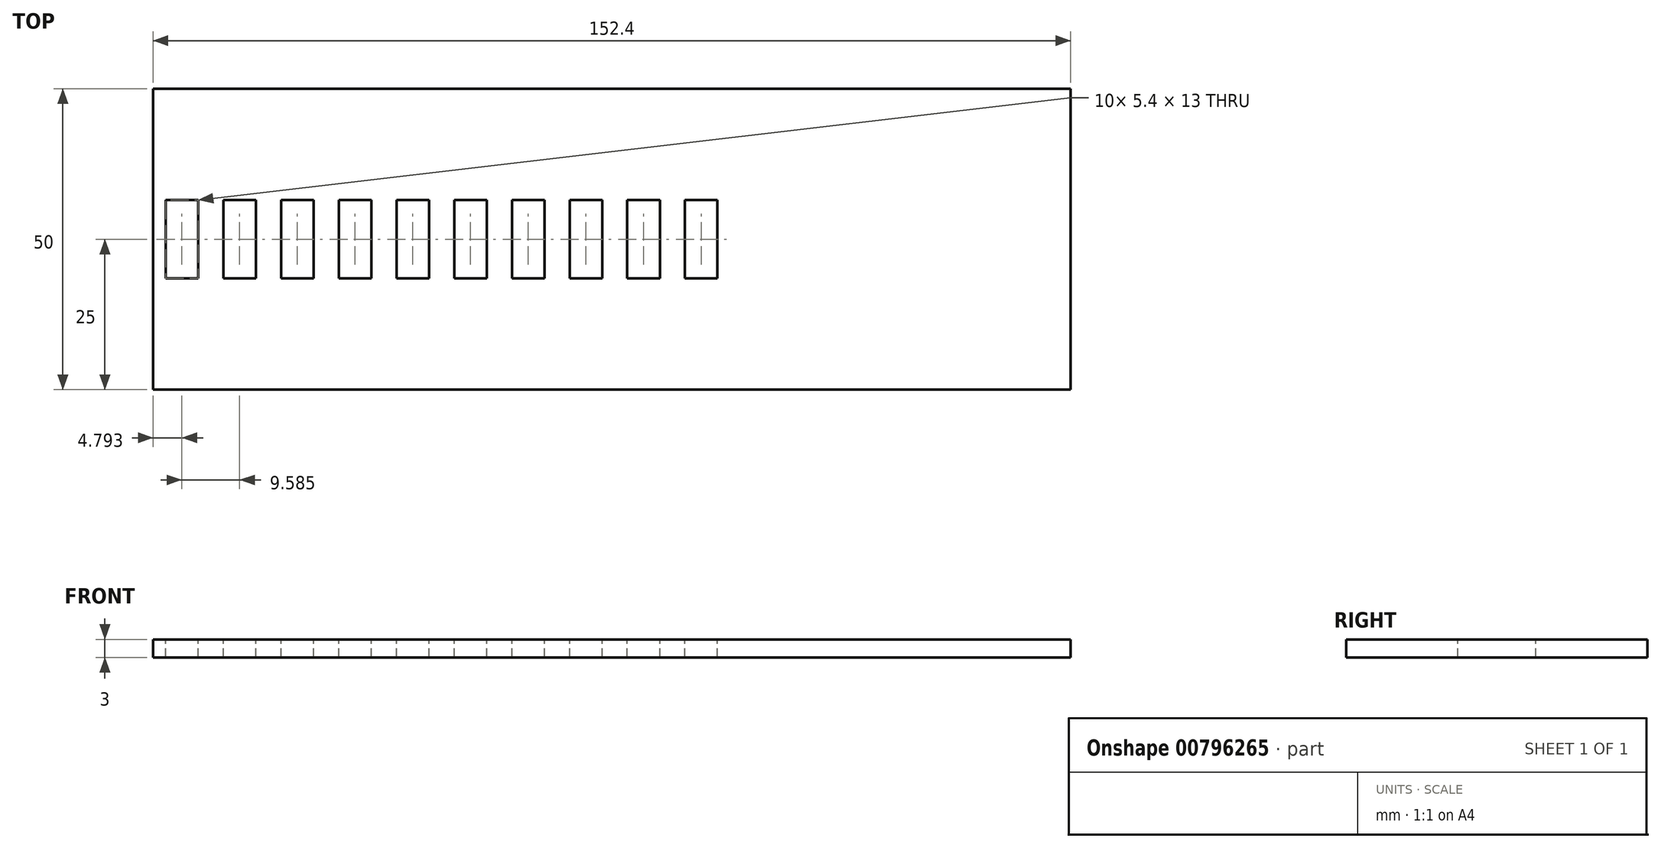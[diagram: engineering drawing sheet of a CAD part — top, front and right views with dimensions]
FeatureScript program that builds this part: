
annotation { "Feature Type Name" : "Feature", "Feature Type Description" : "" }
export const myFeature = defineFeature(function(context is Context, id is Id, definition is map)
    precondition{}
    {
        {
            var Q0;
            Q0=qCreatedBy(makeId("Top.planeOp"),FACE);
            var sketch = newSketch(context, id + "F0", { "sketchPlane" : qUnion([Q0])});
            skLineSegment(sketch, "E0.bottom", {"start": v(76.2, -25) * mm, "end": v(-76.2, -25) * mm});
            skLineSegment(sketch, "E0.top", {"start": v(76.2, 25) * mm, "end": v(-76.2, 25) * mm});
            skLineSegment(sketch, "E0.left", {"start": v(76.2, -25) * mm, "end": v(76.2, 25) * mm});
            skLineSegment(sketch, "E0.right", {"start": v(-76.2, -25) * mm, "end": v(-76.2, 25) * mm});
            skPoint(sketch, "E0.middle", {"position": v(0, 0) * mm});
            skSolve(sketch);
        }
        {
            var Q0;
            Q0 = qSketchRegion(id + "F0", true);
            extrude(context, id + "F1", {"entities" : qUnion([Q0]), "depth" : 3 * mm, "offsetDistance" : 25.4 * mm});
        }
        {
            var Q0;
            Q0=makeQuery(id+"F1.opExtrude","CAP_FACE",FACE,{"disambiguationData":[OSD([sQuery(id+"F0.wireOp",EDGE,"E0.bottom"),sQuery(id+"F0.wireOp",EDGE,"E0.top"),sQuery(id+"F0.wireOp",EDGE,"E0.left"),sQuery(id+"F0.wireOp",EDGE,"E0.right")])],"isStart":false});
            var sketch = newSketch(context, id + "F2", { "sketchPlane" : qUnion([Q0])});
            skLineSegment(sketch, "E1", {"start": v(-76.2, 0) * mm, "end": v(76.2, 0) * mm, "construction": true});
            skLineSegment(sketch, "E2.bottom", {"start": v(-68.7, -6.5) * mm, "end": v(-74.1, -6.5) * mm});
            skLineSegment(sketch, "E2.top", {"start": v(-68.7, 6.5) * mm, "end": v(-74.1, 6.5) * mm});
            skLineSegment(sketch, "E2.left", {"start": v(-68.7, -6.5) * mm, "end": v(-68.7, 6.5) * mm});
            skLineSegment(sketch, "E2.right", {"start": v(-74.1, -6.5) * mm, "end": v(-74.1, 6.5) * mm});
            skPoint(sketch, "E2.middle", {"position": v(-71.4, 0) * mm});
            skLineSegment(sketch, "E3.1.0.0", {"start": v(-59.12, 6.5) * mm, "end": v(-64.52, 6.5) * mm});
            skLineSegment(sketch, "E3.1.0.1", {"start": v(-64.52, -6.5) * mm, "end": v(-64.52, 6.5) * mm});
            skLineSegment(sketch, "E3.1.0.2", {"start": v(-59.12, -6.5) * mm, "end": v(-59.12, 6.5) * mm});
            skLineSegment(sketch, "E3.1.0.3", {"start": v(-59.12, -6.5) * mm, "end": v(-64.52, -6.5) * mm});
            skLineSegment(sketch, "E3.2.0.0", {"start": v(-49.54, 6.5) * mm, "end": v(-54.94, 6.5) * mm});
            skLineSegment(sketch, "E3.2.0.1", {"start": v(-54.94, -6.5) * mm, "end": v(-54.94, 6.5) * mm});
            skLineSegment(sketch, "E3.2.0.2", {"start": v(-49.54, -6.5) * mm, "end": v(-49.54, 6.5) * mm});
            skLineSegment(sketch, "E3.2.0.3", {"start": v(-49.54, -6.5) * mm, "end": v(-54.94, -6.5) * mm});
            skLineSegment(sketch, "E3.3.0.0", {"start": v(-39.95, 6.5) * mm, "end": v(-45.35, 6.5) * mm});
            skLineSegment(sketch, "E3.3.0.1", {"start": v(-45.35, -6.5) * mm, "end": v(-45.35, 6.5) * mm});
            skLineSegment(sketch, "E3.3.0.2", {"start": v(-39.95, -6.5) * mm, "end": v(-39.95, 6.5) * mm});
            skLineSegment(sketch, "E3.3.0.3", {"start": v(-39.95, -6.5) * mm, "end": v(-45.35, -6.5) * mm});
            skLineSegment(sketch, "E3.4.0.0", {"start": v(-30.37, 6.5) * mm, "end": v(-35.77, 6.5) * mm});
            skLineSegment(sketch, "E3.4.0.1", {"start": v(-35.77, -6.5) * mm, "end": v(-35.77, 6.5) * mm});
            skLineSegment(sketch, "E3.4.0.2", {"start": v(-30.37, -6.5) * mm, "end": v(-30.37, 6.5) * mm});
            skLineSegment(sketch, "E3.4.0.3", {"start": v(-30.37, -6.5) * mm, "end": v(-35.77, -6.5) * mm});
            skLineSegment(sketch, "E3.5.0.0", {"start": v(-20.78, 6.5) * mm, "end": v(-26.18, 6.5) * mm});
            skLineSegment(sketch, "E3.5.0.1", {"start": v(-26.18, -6.5) * mm, "end": v(-26.18, 6.5) * mm});
            skLineSegment(sketch, "E3.5.0.2", {"start": v(-20.78, -6.5) * mm, "end": v(-20.78, 6.5) * mm});
            skLineSegment(sketch, "E3.5.0.3", {"start": v(-20.78, -6.5) * mm, "end": v(-26.18, -6.5) * mm});
            skLineSegment(sketch, "E3.6.0.0", {"start": v(-11.2, 6.5) * mm, "end": v(-16.6, 6.5) * mm});
            skLineSegment(sketch, "E3.6.0.1", {"start": v(-16.6, -6.5) * mm, "end": v(-16.6, 6.5) * mm});
            skLineSegment(sketch, "E3.6.0.2", {"start": v(-11.2, -6.5) * mm, "end": v(-11.2, 6.5) * mm});
            skLineSegment(sketch, "E3.6.0.3", {"start": v(-11.2, -6.5) * mm, "end": v(-16.6, -6.5) * mm});
            skLineSegment(sketch, "E3.7.0.0", {"start": v(-1.61, 6.5) * mm, "end": v(-7.01, 6.5) * mm});
            skLineSegment(sketch, "E3.7.0.1", {"start": v(-7.01, -6.5) * mm, "end": v(-7.01, 6.5) * mm});
            skLineSegment(sketch, "E3.7.0.2", {"start": v(-1.61, -6.5) * mm, "end": v(-1.61, 6.5) * mm});
            skLineSegment(sketch, "E3.7.0.3", {"start": v(-1.61, -6.5) * mm, "end": v(-7.01, -6.5) * mm});
            skLineSegment(sketch, "E3.8.0.0", {"start": v(7.97, 6.5) * mm, "end": v(2.57, 6.5) * mm});
            skLineSegment(sketch, "E3.8.0.1", {"start": v(2.57, -6.5) * mm, "end": v(2.57, 6.5) * mm});
            skLineSegment(sketch, "E3.8.0.2", {"start": v(7.97, -6.5) * mm, "end": v(7.97, 6.5) * mm});
            skLineSegment(sketch, "E3.8.0.3", {"start": v(7.97, -6.5) * mm, "end": v(2.57, -6.5) * mm});
            skLineSegment(sketch, "E3.9.0.0", {"start": v(17.56, 6.5) * mm, "end": v(12.16, 6.5) * mm});
            skLineSegment(sketch, "E3.9.0.1", {"start": v(12.16, -6.5) * mm, "end": v(12.16, 6.5) * mm});
            skLineSegment(sketch, "E3.9.0.2", {"start": v(17.56, -6.5) * mm, "end": v(17.56, 6.5) * mm});
            skLineSegment(sketch, "E3.9.0.3", {"start": v(17.56, -6.5) * mm, "end": v(12.16, -6.5) * mm});
            skLineSegment(sketch, "E3.direction1", {"start": v(-74.1, 6.5) * mm, "end": v(-64.52, 6.5) * mm, "construction": true});
            skSolve(sketch);
        }
        {
            var Q0;
            Q0 = qSketchRegion(id + "F2", true);
            extrude(context, id + "F3", {"entities" : qUnion([Q0]), "operationType" : NewBodyOperationType.REMOVE, "endBound" : BoundingType.THROUGH_ALL, "oppositeDirection" : true, "depth" : 25 * mm, "offsetDistance" : 25 * mm});
        }
    });
